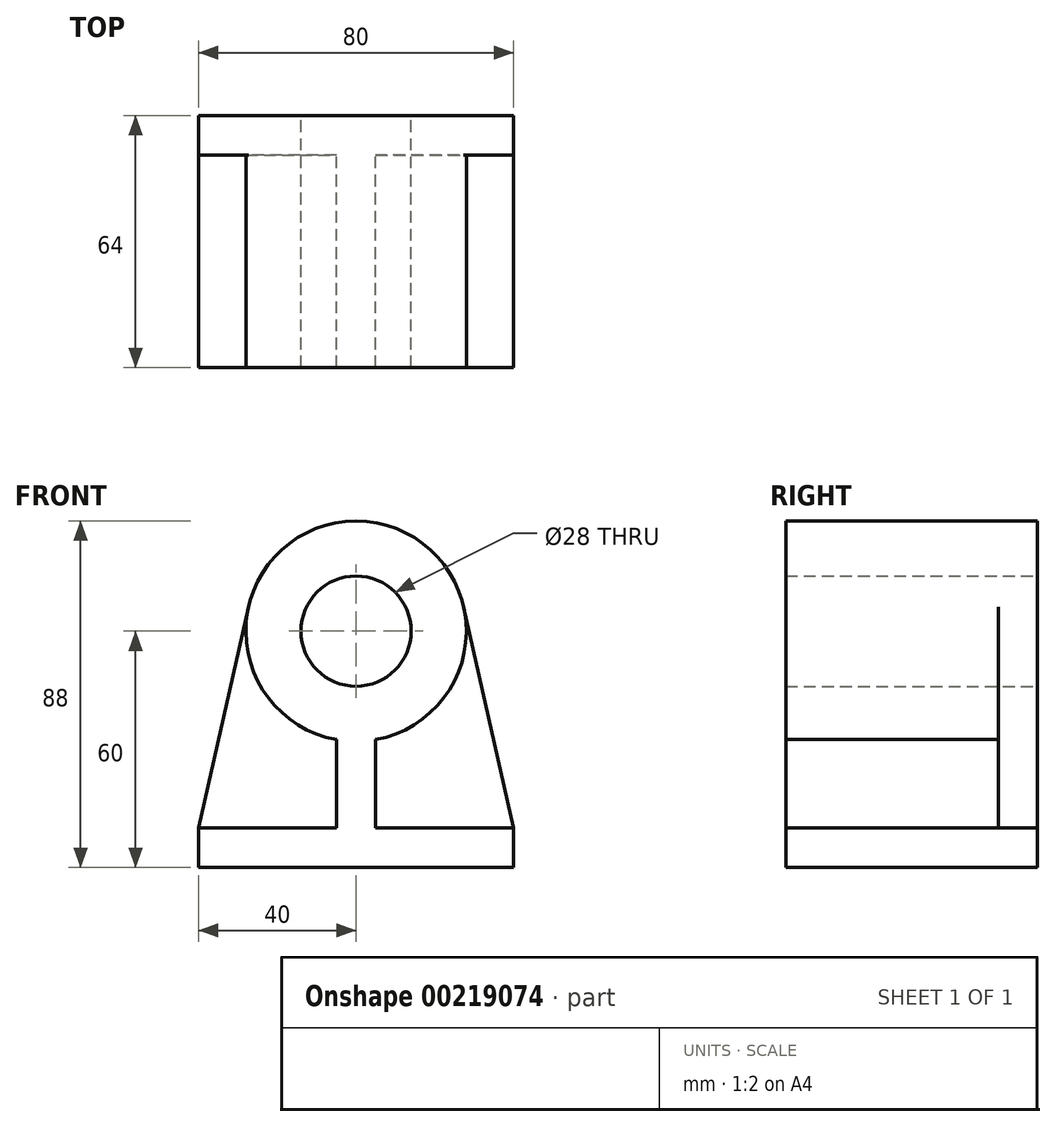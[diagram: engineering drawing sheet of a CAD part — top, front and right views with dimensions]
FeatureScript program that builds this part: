
annotation { "Feature Type Name" : "Feature", "Feature Type Description" : "" }
export const myFeature = defineFeature(function(context is Context, id is Id, definition is map)
    precondition{}
    {
        {
            var Q0;
            Q0=qCreatedBy(makeId("Front.planeOp"),FACE);
            var sketch = newSketch(context, id + "F0", { "sketchPlane" : qUnion([Q0])});
            skLineSegment(sketch, "E0", {"start": v(0, 0) * mm, "end": v(80, 0) * mm});
            skLineSegment(sketch, "E1", {"start": v(80, 0) * mm, "end": v(80, 10) * mm});
            skLineSegment(sketch, "E2", {"start": v(80, 10) * mm, "end": v(45, 10) * mm});
            skLineSegment(sketch, "E3", {"start": v(45, 10) * mm, "end": v(45, 32.45) * mm});
            skLineSegment(sketch, "E4", {"start": v(35, 32.45) * mm, "end": v(35, 10) * mm});
            skLineSegment(sketch, "E5", {"start": v(35, 10) * mm, "end": v(0, 10) * mm});
            skLineSegment(sketch, "E6", {"start": v(0, 10) * mm, "end": v(0, 0) * mm});
            skArc(sketch, "E7", {"start": v(45, 32.45) * mm, "mid": v(40, 88) * mm, "end": v(35, 32.45) * mm});
            skCircle(sketch, "E8", {"center": v(40, 60) * mm, "radius": 14 * mm});
            skLineSegment(sketch, "E9", {"start": v(40, 97.69) * mm, "end": v(40, -31.75) * mm, "construction": true});
            skLineSegment(sketch, "E10", {"start": v(0, 10) * mm, "end": v(12.69, 66.17) * mm});
            skLineSegment(sketch, "E11", {"start": v(80, 10) * mm, "end": v(67.31, 66.17) * mm});
            skSolve(sketch);
        }
        {
            var Q0;
            Q0=makeQuery(id+"F0.imprint","IMPRINT",FACE,{"disambiguationData":[TD([[makeQuery(id+"F0.imprint","IMPRINT",EDGE,{"derivedFrom":sQuery(id+"F0.wireOp",EDGE,"E0")}),1.0]])]});
            extrude(context, id + "F1", {"entities" : qUnion([Q0]), "depth" : 64 * mm});
        }
        {
            var Q0;
            Q0=makeQuery(id+"F0.imprint","IMPRINT",FACE,{"disambiguationData":[TD([[makeQuery(id+"F0.imprint","IMPRINT",EDGE,{"derivedFrom":sQuery(id+"F0.wireOp",EDGE,"E2")}),-1.0]])]});
            var Q1;
            {var subQ0=sQuery(id+"F0.wireOp",EDGE,"E4");Q1=makeQuery(id+"F0.imprint","IMPRINT",FACE,{"disambiguationData":[TD([[makeQuery(id+"F0.imprint","IMPRINT",EDGE,{"derivedFrom":subQ0}),-1.0]])]});}
            extrude(context, id + "F2", {"entities" : qUnion([Q0, Q1]), "operationType" : NewBodyOperationType.ADD, "depth" : 10 * mm});
        }
    });
